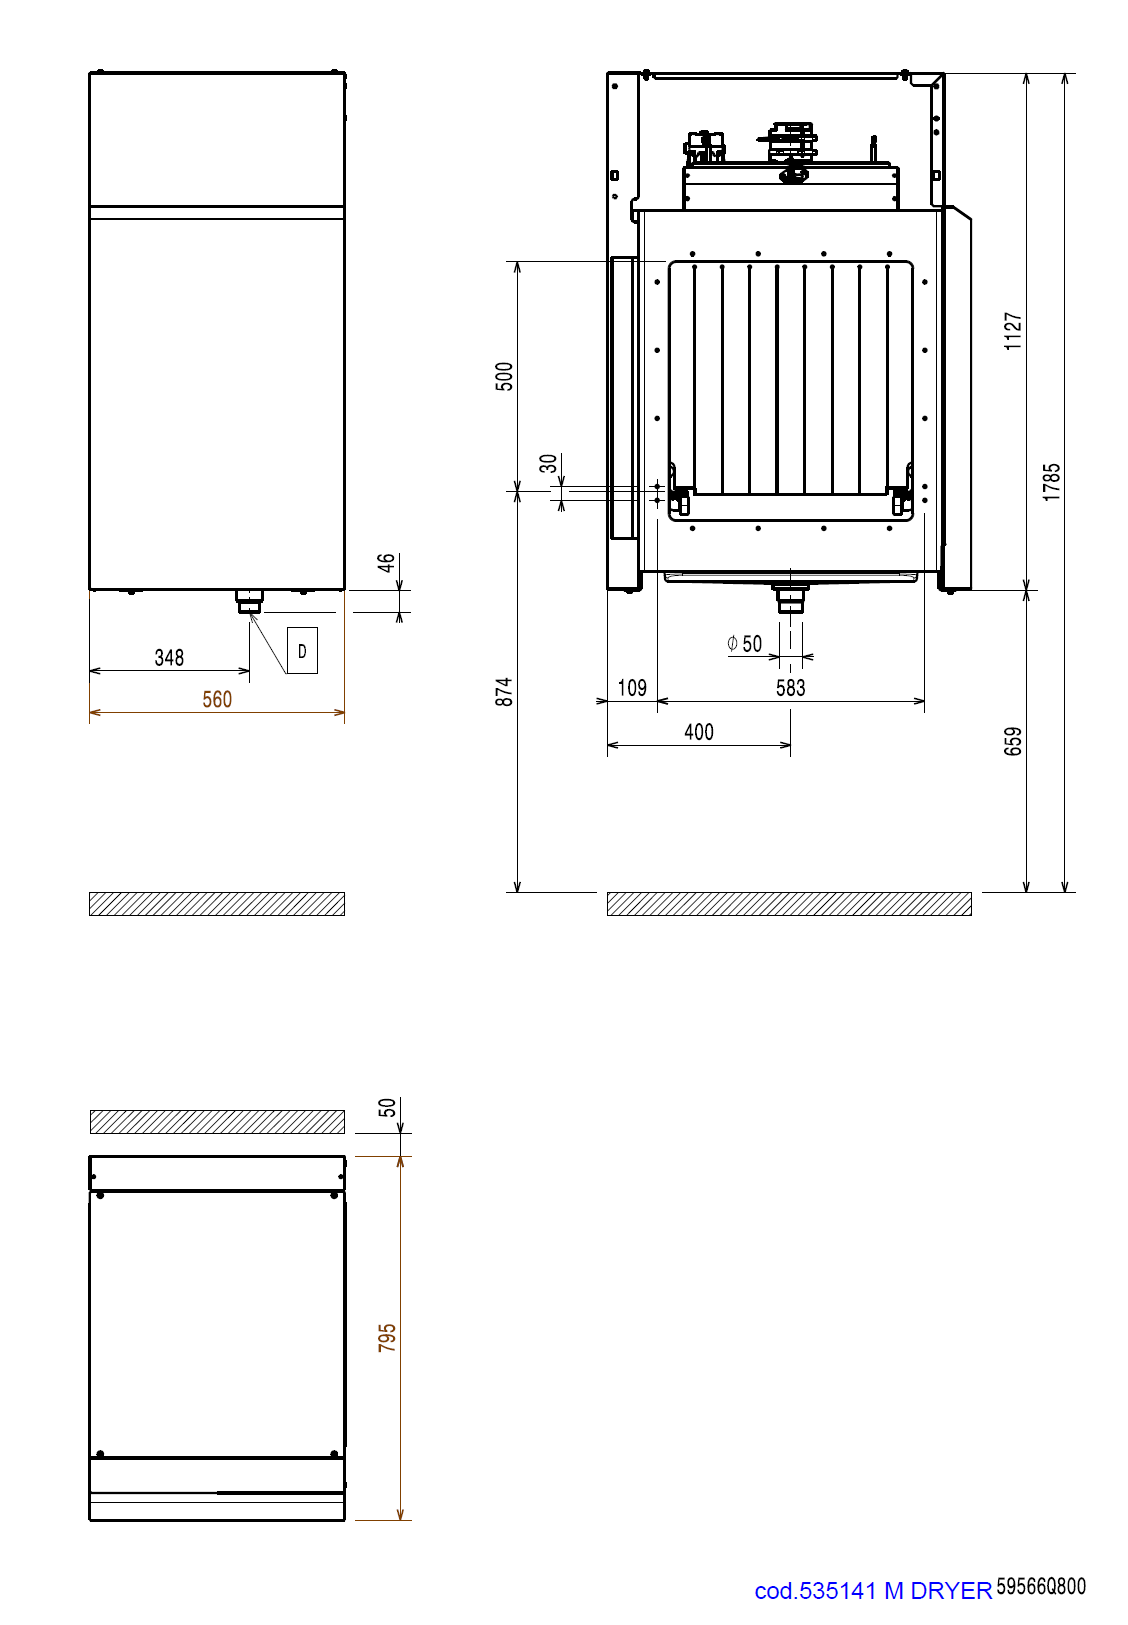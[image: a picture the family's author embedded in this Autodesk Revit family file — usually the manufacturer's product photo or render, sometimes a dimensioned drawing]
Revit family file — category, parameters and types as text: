
# Revit family: QF_ELECTROLUXPROFESSIONAL_535141_NMHDRE56
name_source: partatom
category: Specialty Equipment
revit_build: Autodesk Revit 2018 (Build: 20190510_1515(x64)
units: mm (PartAtom-declared; Revit-internal decimal feet)

## family parameters
Always vertical = Yes
Cut with Voids When Loaded = No
Part Type = Normal
Room Calculation Point = No
Round Connector Dimension = Use Diameter
Shared = No
Work Plane-Based = No

## types (2) — shared parameters
Accessory = Yes
Cold Water Size = 0 mm
Compressed Air Pressure = 0.0 Pa
Compressed Air Size = 0 mm
Compressed Air Volume = 0.0 L/s
Condensate Return Size = 0 mm
Depth Actual = 795 mm  [stored 2.60827 ft]
Direct Waste Size = 50 mm
Gas Input Pressure = 0
Gas Size = 0 mm
HP = 5.9 HP
Height Actual = 1130 mm  [stored 3.70735 ft]
Hot Water Size = 0 mm
Length Actual = 560 mm  [stored 1.83727 ft]
Refrigerant Compressor Remote = Yes
Refrigeration Liquid Line Size = 0 mm
Refrigeration Suction Line Size = 0 mm
Steam Supply Maximum Pressure = 0.0 Pa
Steam Supply Minimum Pressure = 0.0 Pa
Steam Supply Size = 0 mm
URL = http://professional.electrolux.com
Watts = 0 W
Weight = 0.00 kg
zero-valued in all types: Gas KW, Steam Pounds per Hour

## per-type parameters (varying)
| type | Cycle | Description | Item Number | Manufacturer | Model | Phase | URL Manufacturer | Volts |
| NMHDRE56 | 0 Hz | SINGLE RINSE RT, 100R/H, ELECTRIC 50HZ |  | Electrolux | ESR10E5 | 0 |  | 0 V |
| Standard | 60 Hz | MEDIUM DRYER WITHOUT DOOR (HAB) FOR DUAL RINSE RT, ELECTRIC, 50HZ & 60HZ | 535141 | Electrolux Professional | NMHDRE56 | 3 | http://professional.electrolux.com | 380 V |

note: source unit labels omitted for Gas Input Pressure — the stored unit's dimension contradicts the parameter name (converter mislabeling)

note: [stored X ft] marks values corroborated as IEEE doubles in the binary element streams (Revit-internal decimal feet)
